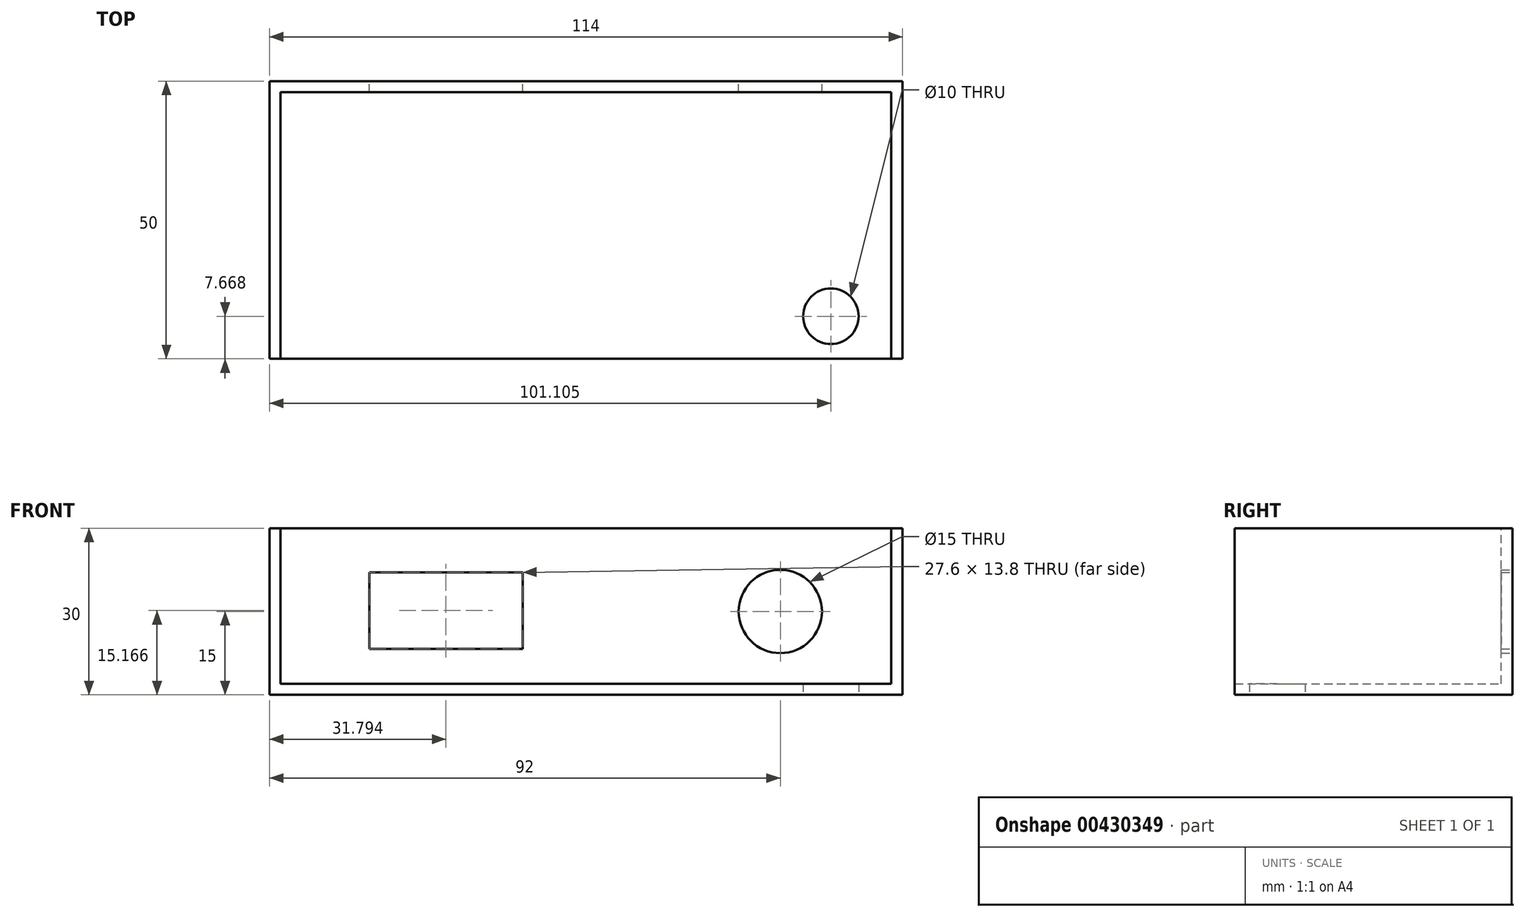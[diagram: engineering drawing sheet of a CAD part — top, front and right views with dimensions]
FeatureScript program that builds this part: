
annotation { "Feature Type Name" : "Feature", "Feature Type Description" : "" }
export const myFeature = defineFeature(function(context is Context, id is Id, definition is map)
    precondition{}
    {
        {
            var Q0;
            Q0=qCreatedBy(makeId("Front.planeOp"),FACE);
            var sketch = newSketch(context, id + "F0", { "sketchPlane" : qUnion([Q0])});
            skLineSegment(sketch, "E0.bottom", {"start": v(0, 0) * mm, "end": v(114, 0) * mm});
            skLineSegment(sketch, "E0.top", {"start": v(0, 30) * mm, "end": v(114, 30) * mm});
            skLineSegment(sketch, "E0.left", {"start": v(0, 0) * mm, "end": v(0, 30) * mm});
            skLineSegment(sketch, "E0.right", {"start": v(114, 0) * mm, "end": v(114, 30) * mm});
            skCircle(sketch, "E1", {"center": v(92, 15) * mm, "radius": 7.5 * mm});
            skLineSegment(sketch, "E2.bottom", {"start": v(45.6, 22.07) * mm, "end": v(18, 22.07) * mm});
            skLineSegment(sketch, "E2.top", {"start": v(45.6, 8.27) * mm, "end": v(18, 8.27) * mm});
            skLineSegment(sketch, "E2.left", {"start": v(45.6, 22.07) * mm, "end": v(45.6, 8.27) * mm});
            skLineSegment(sketch, "E2.right", {"start": v(18, 22.07) * mm, "end": v(18, 8.27) * mm});
            skPoint(sketch, "E2.middle", {"position": v(31.8, 15.17) * mm});
            skLineSegment(sketch, "E3.0", {"start": v(2, 2) * mm, "end": v(2, 30) * mm});
            skLineSegment(sketch, "E3.1", {"start": v(2, 2) * mm, "end": v(112, 2) * mm});
            skLineSegment(sketch, "E3.2", {"start": v(112, 2) * mm, "end": v(112, 30) * mm});
            skSolve(sketch);
        }
        {
            var Q0;
            Q0=makeQuery(id+"F0.imprint","IMPRINT",FACE,{"disambiguationData":[TD([[makeQuery(id+"F0.imprint","IMPRINT",EDGE,{"derivedFrom":sQuery(id+"F0.wireOp",EDGE,"E0.bottom")}),1.0]])]});
            extrude(context, id + "F1", {"entities" : qUnion([Q0]), "depth" : 50 * mm});
        }
        {
            var Q0;
            Q0=makeQuery(id+"F0.imprint","IMPRINT",FACE,{"disambiguationData":[TD([[makeQuery(id+"F0.imprint","IMPRINT",EDGE,{"derivedFrom":sQuery(id+"F0.wireOp",EDGE,"E1")}),-1.0]])]});
            extrude(context, id + "F2", {"entities" : qUnion([Q0]), "operationType" : NewBodyOperationType.ADD, "depth" : 2 * mm});
        }
        {
            var Q0;
            Q0=qCreatedBy(makeId("Top.planeOp"),FACE);
            var sketch = newSketch(context, id + "F3", { "sketchPlane" : qUnion([Q0])});
            skLineSegment(sketch, "E4.bottom", {"start": v(0, 0) * mm, "end": v(114, 0) * mm});
            skLineSegment(sketch, "E4.top", {"start": v(0, -50) * mm, "end": v(114, -50) * mm});
            skLineSegment(sketch, "E4.left", {"start": v(0, 0) * mm, "end": v(0, -50) * mm});
            skLineSegment(sketch, "E4.right", {"start": v(114, 0) * mm, "end": v(114, -50) * mm});
            skCircle(sketch, "E5", {"center": v(101.1, -42.33) * mm, "radius": 5 * mm});
            skSolve(sketch);
        }
        {
            var Q0;
            Q0=sQuery(id+"F3.wireOp",VERTEX,"E5.center");
            var Q1;
            Q1=makeQuery(id+"F1.opExtrude","SWEPT_BODY",BODY,{"disambiguationData":[OSD([sQuery(id+"F0.wireOp",EDGE,"E0.bottom"),sQuery(id+"F0.wireOp",EDGE,"E0.top"),sQuery(id+"F0.wireOp",EDGE,"E0.left"),sQuery(id+"F0.wireOp",EDGE,"E0.right"),sQuery(id+"F0.wireOp",EDGE,"E3.0"),sQuery(id+"F0.wireOp",EDGE,"E3.1"),sQuery(id+"F0.wireOp",EDGE,"E3.2")])]});
            hole(context, id + "F4", {"style" : HoleStyle.SIMPLE, "endStyle" : HoleEndStyle.THROUGH, "oppositeDirection" : true, "holeDiameter" : 10 * mm, "isTappedThrough" : true, "tappedDepth" : 12 * mm, "tapClearance" : 3, "locations" : qUnion([Q0]), "scope" : qUnion([Q1])});
        }
    });
